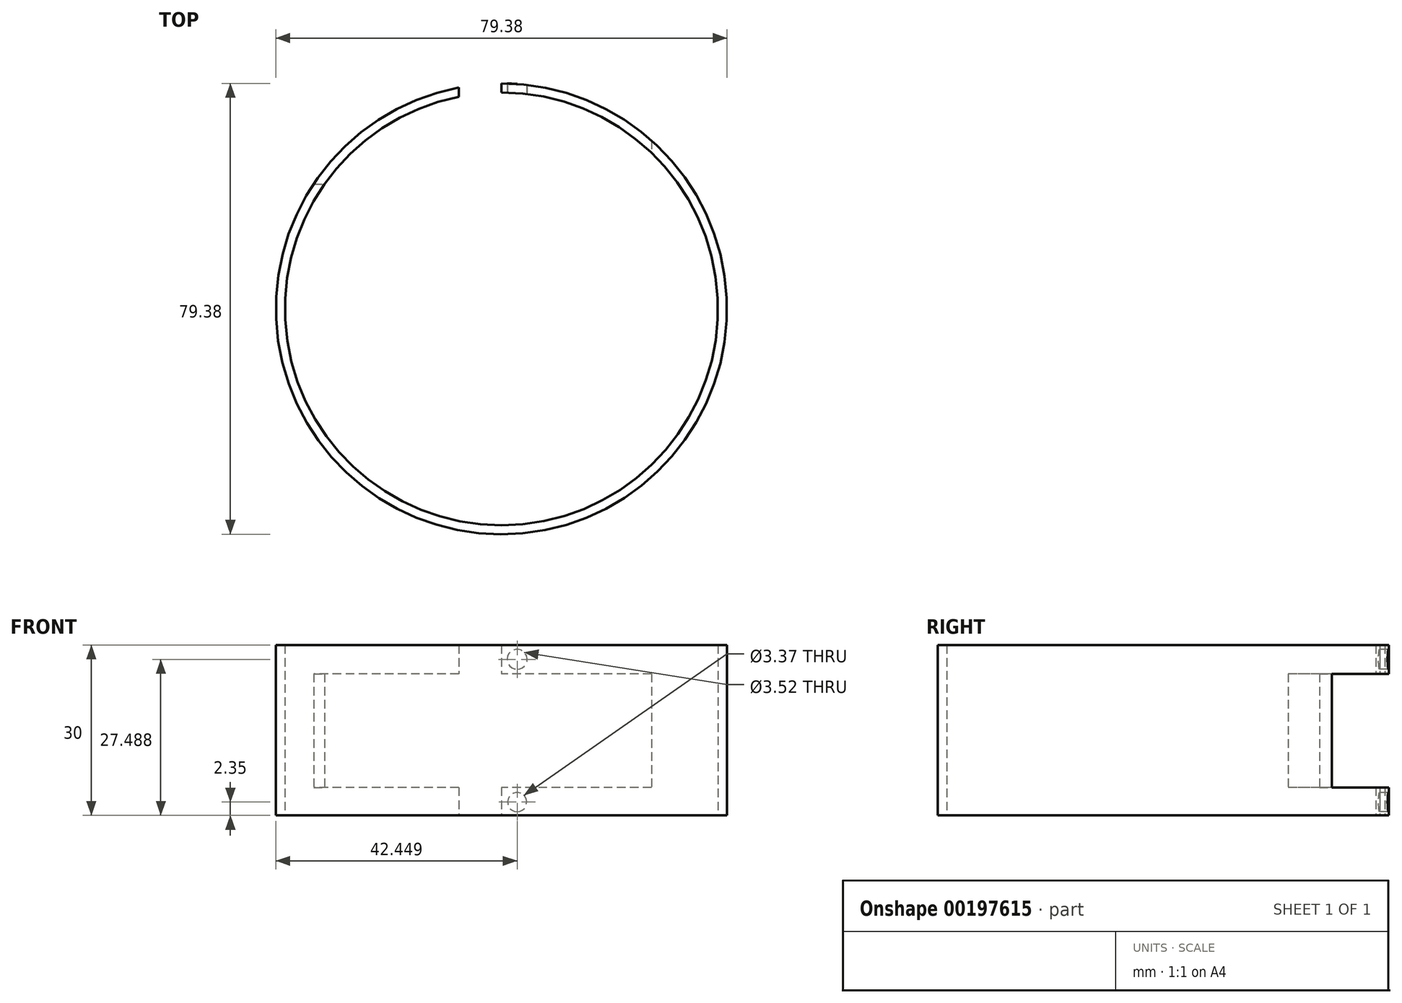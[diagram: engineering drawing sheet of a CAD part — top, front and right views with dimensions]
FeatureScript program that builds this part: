
annotation { "Feature Type Name" : "Feature", "Feature Type Description" : "" }
export const myFeature = defineFeature(function(context is Context, id is Id, definition is map)
    precondition{}
    {
        {
            var Q0;
            Q0=qCreatedBy(makeId("Top.planeOp"),FACE);
            var sketch = newSketch(context, id + "F0", { "sketchPlane" : qUnion([Q0])});
            skCircle(sketch, "E0", {"center": v(0, 0) * mm, "radius": 39.69 * mm});
            skCircle(sketch, "E1", {"center": v(0, 0) * mm, "radius": 38.1 * mm});
            skSolve(sketch);
        }
        {
            var Q0;
            Q0=makeQuery(id+"F0.imprint","IMPRINT",FACE,{"disambiguationData":[TD([[makeQuery(id+"F0.imprint","IMPRINT",EDGE,{"derivedFrom":sQuery(id+"F0.wireOp",EDGE,"E0")}),1.0]])]});
            extrude(context, id + "F1", {"entities" : qUnion([Q0]), "depth" : 30 * mm});
        }
        {
            var Q0;
            Q0=qCreatedBy(makeId("Right.planeOp"),FACE);
            var sketch = newSketch(context, id + "F2", { "sketchPlane" : qUnion([Q0])});
            skLineSegment(sketch, "E2.bottom", {"start": v(46.97, 24.92) * mm, "end": v(21.97, 24.92) * mm});
            skLineSegment(sketch, "E2.top", {"start": v(46.97, 4.92) * mm, "end": v(21.97, 4.92) * mm});
            skLineSegment(sketch, "E2.left", {"start": v(46.97, 24.92) * mm, "end": v(46.97, 4.92) * mm});
            skLineSegment(sketch, "E2.right", {"start": v(21.97, 24.92) * mm, "end": v(21.97, 4.92) * mm});
            skSolve(sketch);
        }
        {
            var Q0;
            Q0 = qSketchRegion(id + "F2", true);
            extrude(context, id + "F3", {"entities" : qUnion([Q0]), "operationType" : NewBodyOperationType.REMOVE, "oppositeDirection" : true, "depth" : 37.85 * mm, "hasSecondDirection" : true, "secondDirectionOppositeDirection" : false, "secondDirectionDepth" : 26.42 * mm});
        }
        {
            var Q0;
            Q0=qCreatedBy(makeId("Right.planeOp"),FACE);
            var sketch = newSketch(context, id + "F4", { "sketchPlane" : qUnion([Q0])});
            skLineSegment(sketch, "E3.bottom", {"start": v(2.15, 33) * mm, "end": v(-3.17, 33) * mm});
            skLineSegment(sketch, "E3.top", {"start": v(2.15, -3.78) * mm, "end": v(-3.17, -3.78) * mm});
            skLineSegment(sketch, "E3.left", {"start": v(2.15, 33) * mm, "end": v(2.15, -3.78) * mm});
            skLineSegment(sketch, "E3.right", {"start": v(-3.17, 33) * mm, "end": v(-3.17, -3.78) * mm});
            skLineSegment(sketch, "E4.bottom", {"start": v(67.74, 59.66) * mm, "end": v(31.2, 59.66) * mm});
            skLineSegment(sketch, "E4.top", {"start": v(67.74, -3.78) * mm, "end": v(31.2, -3.78) * mm});
            skLineSegment(sketch, "E4.left", {"start": v(67.74, 59.66) * mm, "end": v(67.74, -3.78) * mm});
            skLineSegment(sketch, "E4.right", {"start": v(31.2, 59.66) * mm, "end": v(31.2, -3.78) * mm});
            skSolve(sketch);
        }
        {
            var Q0;
            Q0=makeQuery(id+"F4.imprint","IMPRINT",FACE,{"disambiguationData":[TD([[makeQuery(id+"F4.imprint","IMPRINT",EDGE,{"derivedFrom":sQuery(id+"F4.wireOp",EDGE,"E4.bottom")}),1.0]])]});
            extrude(context, id + "F5", {"entities" : qUnion([Q0]), "operationType" : NewBodyOperationType.REMOVE, "oppositeDirection" : true, "depth" : 7.5 * mm});
        }
        {
            var Q0;
            Q0=qCreatedBy(makeId("Front.planeOp"),FACE);
            var sketch = newSketch(context, id + "F6", { "sketchPlane" : qUnion([Q0])});
            skCircle(sketch, "E5", {"center": v(-17.54, -25.16) * mm, "radius": 1.72 * mm});
            skCircle(sketch, "E6", {"center": v(-17.54, 0) * mm, "radius": 2.04 * mm});
            skSolve(sketch);
        }
        {
            var Q0;
            Q0=makeQuery(id+"F6.imprint","IMPRINT",FACE,{"disambiguationData":[TD([[makeQuery(id+"F6.imprint","IMPRINT",EDGE,{"derivedFrom":sQuery(id+"F6.wireOp",EDGE,"E5")}),1.0]])]});
            var Q1;
            Q1=makeQuery(id+"F6.imprint","IMPRINT",FACE,{"disambiguationData":[TD([[makeQuery(id+"F6.imprint","IMPRINT",EDGE,{"derivedFrom":sQuery(id+"F6.wireOp",EDGE,"E6")}),1.0]])]});
            extrude(context, id + "F7", {"entities" : qUnion([Q0, Q1]), "operationType" : NewBodyOperationType.REMOVE, "oppositeDirection" : true, "depth" : 25.4 * mm, "hasSecondDirection" : true, "secondDirectionOppositeDirection" : false, "secondDirectionDepth" : 13.46 * mm});
        }
        {
            var Q0;
            Q0=qCreatedBy(makeId("Front.planeOp"),FACE);
            var sketch = newSketch(context, id + "F8", { "sketchPlane" : qUnion([Q0])});
            skCircle(sketch, "E7", {"center": v(2.76, 27.49) * mm, "radius": 1.76 * mm});
            skCircle(sketch, "E8", {"center": v(2.76, 2.35) * mm, "radius": 1.69 * mm});
            skSolve(sketch);
        }
        {
            var Q0;
            Q0 = qSketchRegion(id + "F8", true);
            extrude(context, id + "F9", {"entities" : qUnion([Q0]), "operationType" : NewBodyOperationType.REMOVE, "oppositeDirection" : true, "depth" : 50 * mm});
        }
    });
